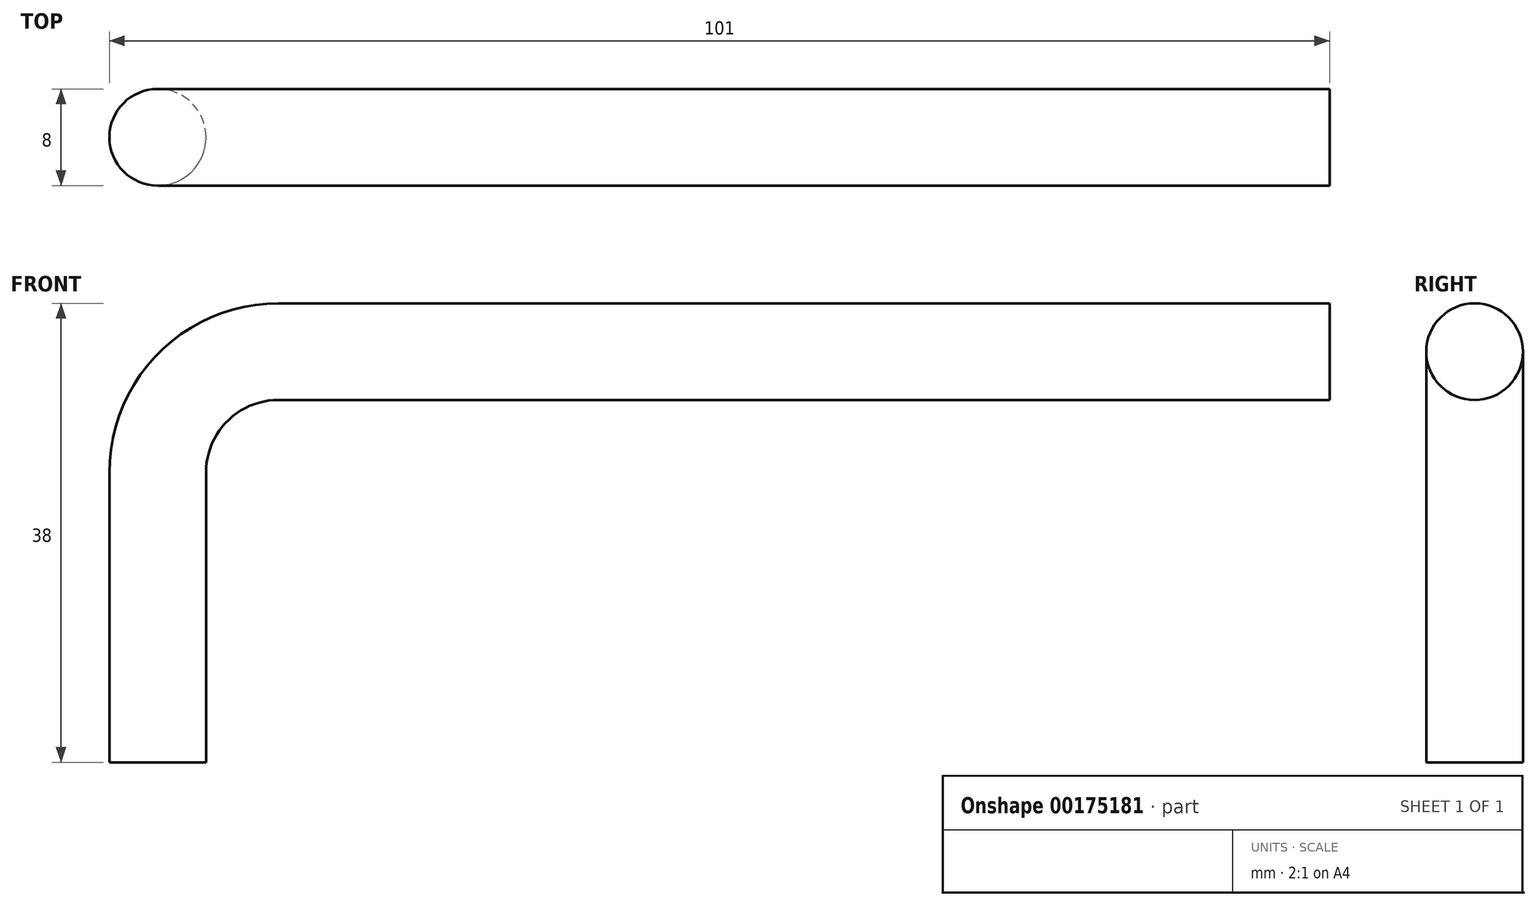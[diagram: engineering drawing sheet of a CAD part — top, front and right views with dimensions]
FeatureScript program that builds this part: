
annotation { "Feature Type Name" : "Feature", "Feature Type Description" : "" }
export const myFeature = defineFeature(function(context is Context, id is Id, definition is map)
    precondition{}
    {
        {
            var Q0;
            Q0=qCreatedBy(makeId("Front.planeOp"),FACE);
            var sketch = newSketch(context, id + "F0", { "sketchPlane" : qUnion([Q0])});
            skLineSegment(sketch, "E0", {"start": v(0, 0) * mm, "end": v(0, 24) * mm});
            skLineSegment(sketch, "E1", {"start": v(10, 34) * mm, "end": v(97, 34) * mm});
            skPoint(sketch, "E2.visualSharp", {"position": v(0, 34) * mm});
            skArc(sketch, "E2.filletArc", {"start": v(10, 34) * mm, "mid": v(2.93, 31.07) * mm, "end": v(0, 24) * mm});
            skSolve(sketch);
        }
        {
            var Q0;
            Q0=qCreatedBy(makeId("Top.planeOp"),FACE);
            var sketch = newSketch(context, id + "F1", { "sketchPlane" : qUnion([Q0])});
            skCircle(sketch, "E3", {"center": v(0, 0) * mm, "radius": 4 * mm});
            skSolve(sketch);
        }
        {
            var Q0;
            Q0 = qSketchRegion(id + "F1", true);
            var Q1;
            Q1 = qConstructionFilter(qBodyType(qCreatedBy(id + "F0" ,EDGE), BodyType.WIRE), ConstructionObject.NO);
            sweep(context, id + "F2", {"profiles" : qUnion([Q0]), "path" : qUnion([Q1])});
        }
    });
